# Revit family: Toilet-Floor_Mount-KOHLER-San_Souci-K-20972T_1
name_source: partatom
category: Plumbing Fixtures
units: mm (PartAtom-declared; Revit-internal decimal feet)

## family parameters
Cut with Voids When Loaded = No
Host = Face
Maintain Annotation Orientation = No
OmniClass Number = 23.31.19.00
OmniClass Title = Toilets
Part Type = Normal
Room Calculation Point = No
Round Connector Dimension = Use Diameter
Shared = No

## types (3) — shared parameters
ADA Compliant = No
Assembly Code = D2010100
Bowl Height = 15 9/16"
CW Connection = Yes
Cold Water Inlet = Cold Water Inlet
Date Modified = 12/02/2022
Default Elevation = 0"
Finish = Kohler-Vitreous_China-0-White
Flow Rate = 0 GPM
HW Connection = No
Height = 24 3/8"
Hot Water Inlet = Hot Water Inlet
Length = 27 1/2"
Manufacturer = Kohler Co.
Master Format 2014 = 22 42 13.13
Master Format 2014 Name = Residential Water Closets
Material = Vitreous China
Pressure = 0.00 psi
Product Name = San Souci
Rough-In = 15 3/4"
Seat Included = Yes
URL = http://www.kohler.com.cn
Vent Connection = No
Waste Connection = Yes
Waste Water Outlet = Waste Water Outlet
WaterSense Certified = No
Width = 16 7/16"

## per-type parameters (varying)
| type | Description | Flush Rate- GPF | Flush Rate- LPF | Model | Product Documentation Link | Product Page URL | Type |
| 1.32 GPF, ITS2, 0-White | C5 360 3.5/5.0L one-piece toilet 400mm | 1.32 GPF | 5.0 LPF | K-20972T-ITS2-0 |  |  | 1 |
| 1.26 GPF, 0-White | C5 360 3.3/4.8L one-piece toilet 400mm | 1.26 GPF | 4.8 LPF | K-20972T-S-0 |  |  | 3 |
| 1.32 GPF, S2, 0-White | Sint Suci skirt version of the one-piece toilet | 1.32 GPF | 5.0 LPF | K-20972T-S2-0 | https://files.kohler.com.cn | https://www.kohler.com.cn | 2 |

## geometry (parser evidence)
native form markers: Sweep x5
no freeform markers — native parametric forms only
